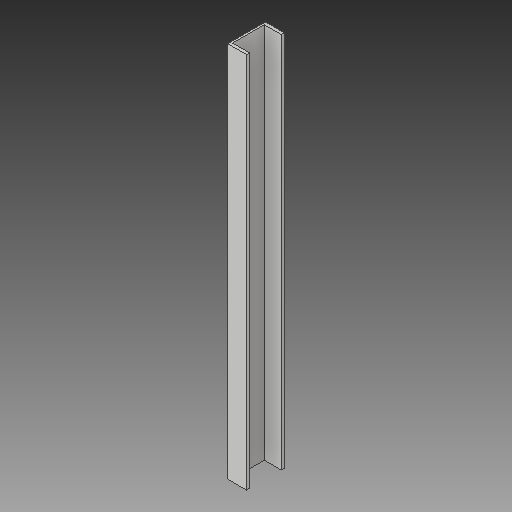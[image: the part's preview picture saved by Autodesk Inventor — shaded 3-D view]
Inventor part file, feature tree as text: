
AUTODESK INVENTOR PART (.ipt)
format: ipt  version: 2019 (Build 230136000, 136)  size: 90,624 bytes
history: native  units: in
note: dims shown in document units (in); Inventor stores cm internally (conversion verified against a paired STEP export)
features: other x3, sketch x1
ambient origin geometry x8: Origin, YZ Plane, XZ Plane, XY Plane, X Axis, Y Axis, Z Axis, Center Point
bodies: Solid1 (feature_tree)
feature tree (4):
  other  "Channel1.ipt"
  other  "Solid1::Channel1.ipt"
  other  "TaggingFeature1"
  sketch  "Sketch1"  dims[d0=0.3937in]
